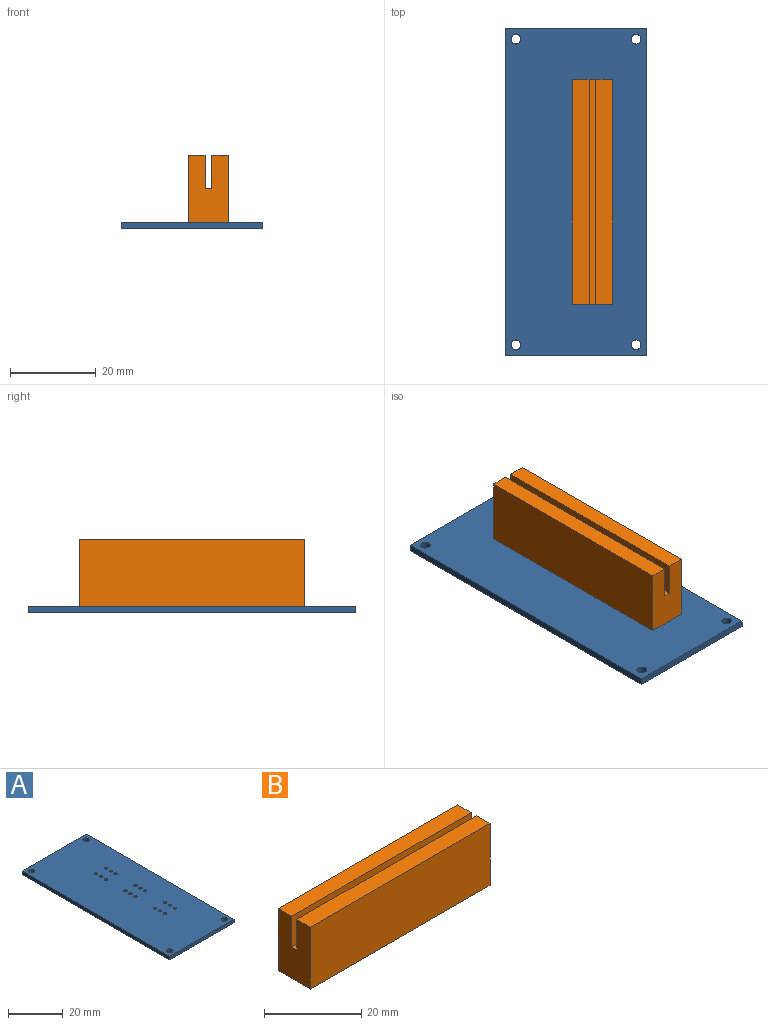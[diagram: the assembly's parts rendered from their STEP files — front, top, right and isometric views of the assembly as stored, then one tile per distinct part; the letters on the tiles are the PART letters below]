
ASSEMBLY  parts=2 mates=1
PART A: 28 faces, bbox 33x76.2x1.6 mm
  f0: plane 33.02x1.6mm, normal (0,-1,0), area 52.8mm2, adj f1,f25,f26,f27
  f1: plane 76.2x1.6mm, normal (1,0,0), area 121.9mm2, adj f0,f2,f26,f27
  f2: plane 33.02x1.6mm, normal (0,1,0), area 52.8mm2, adj f1,f25,f26,f27
  f3: cylinder r=0.64mm len=1.6mm, axis (0,0,-1), area 6.4mm2, adj f26,f27
  f4: cylinder r=0.64mm len=1.6mm, axis (0,0,-1), area 6.4mm2, adj f26,f27
  f5: cylinder r=0.64mm len=1.6mm, axis (0,0,-1), area 6.4mm2, adj f26,f27
  f6: cylinder r=0.64mm len=1.6mm, axis (0,0,-1), area 6.4mm2, adj f26,f27
  f7: cylinder r=0.64mm len=1.6mm, axis (0,0,-1), area 6.4mm2, adj f26,f27
  f8: cylinder r=0.64mm len=1.6mm, axis (0,0,-1), area 6.4mm2, adj f26,f27
  f9: cylinder r=0.64mm len=1.6mm, axis (0,0,-1), area 6.4mm2, adj f26,f27
  f10: cylinder r=0.64mm len=1.6mm, axis (0,0,-1), area 6.4mm2, adj f26,f27
  f11: cylinder r=0.64mm len=1.6mm, axis (0,0,-1), area 6.4mm2, adj f26,f27
  f12: cylinder r=0.64mm len=1.6mm, axis (0,0,-1), area 6.4mm2, adj f26,f27
  f13: cylinder r=0.64mm len=1.6mm, axis (0,0,-1), area 6.4mm2, adj f26,f27
  f14: cylinder r=0.64mm len=1.6mm, axis (0,0,-1), area 6.4mm2, adj f26,f27
  f15: cylinder r=1.14mm len=2.29mm, axis (0,0,-1), area 11.5mm2, adj f26,f27
  f16: cylinder r=1.14mm len=2.29mm, axis (0,0,-1), area 11.5mm2, adj f26,f27
  f17: cylinder r=1.14mm len=2.29mm, axis (0,0,-1), area 11.5mm2, adj f26,f27
  f18: cylinder r=1.14mm len=2.29mm, axis (0,0,-1), area 11.5mm2, adj f26,f27
  f19: cylinder r=0.64mm len=1.6mm, axis (0,0,-1), area 6.4mm2, adj f26,f27
  f20: cylinder r=0.64mm len=1.6mm, axis (0,0,-1), area 6.4mm2, adj f26,f27
  f21: cylinder r=0.64mm len=1.6mm, axis (0,0,-1), area 6.4mm2, adj f26,f27
  f22: cylinder r=0.64mm len=1.6mm, axis (0,0,-1), area 6.4mm2, adj f26,f27
  f23: cylinder r=0.64mm len=1.6mm, axis (0,0,-1), area 6.4mm2, adj f26,f27
  f24: cylinder r=0.64mm len=1.6mm, axis (0,0,-1), area 6.4mm2, adj f26,f27
  f25: plane 76.2x1.6mm, normal (-1,0,0), area 121.9mm2, adj f0,f2,f26,f27
  f26: plane 76.2x33.02mm, normal (0,0,1), area 2476.9mm2, adj f0,f1,f2,f3,f4,f5,f6,f7
  f27: plane 76.2x33.02mm, normal (0,0,-1), area 2476.9mm2, adj f0,f1,f2,f3,f4,f5,f6,f7
PART B: 10 faces, bbox 52.3x9.4x15.6 mm
  f0: plane 52.32x3.92mm, normal (0,0,1), area 205.3mm2, adj f1,f2,f3,f7
  f1: plane 15.6x9.4mm, normal (1,0,0), area 134.7mm2, adj f0,f2,f4,f5,f6,f7,f8,f9
  f2: plane 52.32x15.6mm, normal (0,1,0), area 816.3mm2, adj f0,f1,f3,f6
  f3: plane 15.6x9.4mm, normal (-1,0,0), area 134.7mm2, adj f0,f2,f4,f5,f6,f7,f8,f9
  f4: plane 52.32x15.6mm, normal (0,-1,0), area 816.3mm2, adj f1,f3,f5,f6
  f5: plane 52.32x3.92mm, normal (0,0,1), area 205.3mm2, adj f1,f3,f4,f8
  f6: plane 52.32x9.4mm, normal (0,0,-1), area 491.7mm2, adj f1,f2,f3,f4
  f7: plane 52.32x7.7mm, normal (0,-1,0), area 402.9mm2, adj f0,f1,f3,f9
  f8: plane 52.32x7.7mm, normal (0,1,0), area 402.9mm2, adj f1,f3,f5,f9
  f9: plane 52.32x1.55mm, normal (0,0,1), area 81.1mm2, adj f1,f3,f7,f8
PLACE A t=(-46.01,-83.27,-14.42)mm
PLACE B rot(axis=(0,0,1),90deg) t=(-54.01,-19.01,-12.82)mm
MATE fastened B.f6 <-> A.f26  axis (0,0,-1) through (-58.71,-45.17,-12.82)mm
